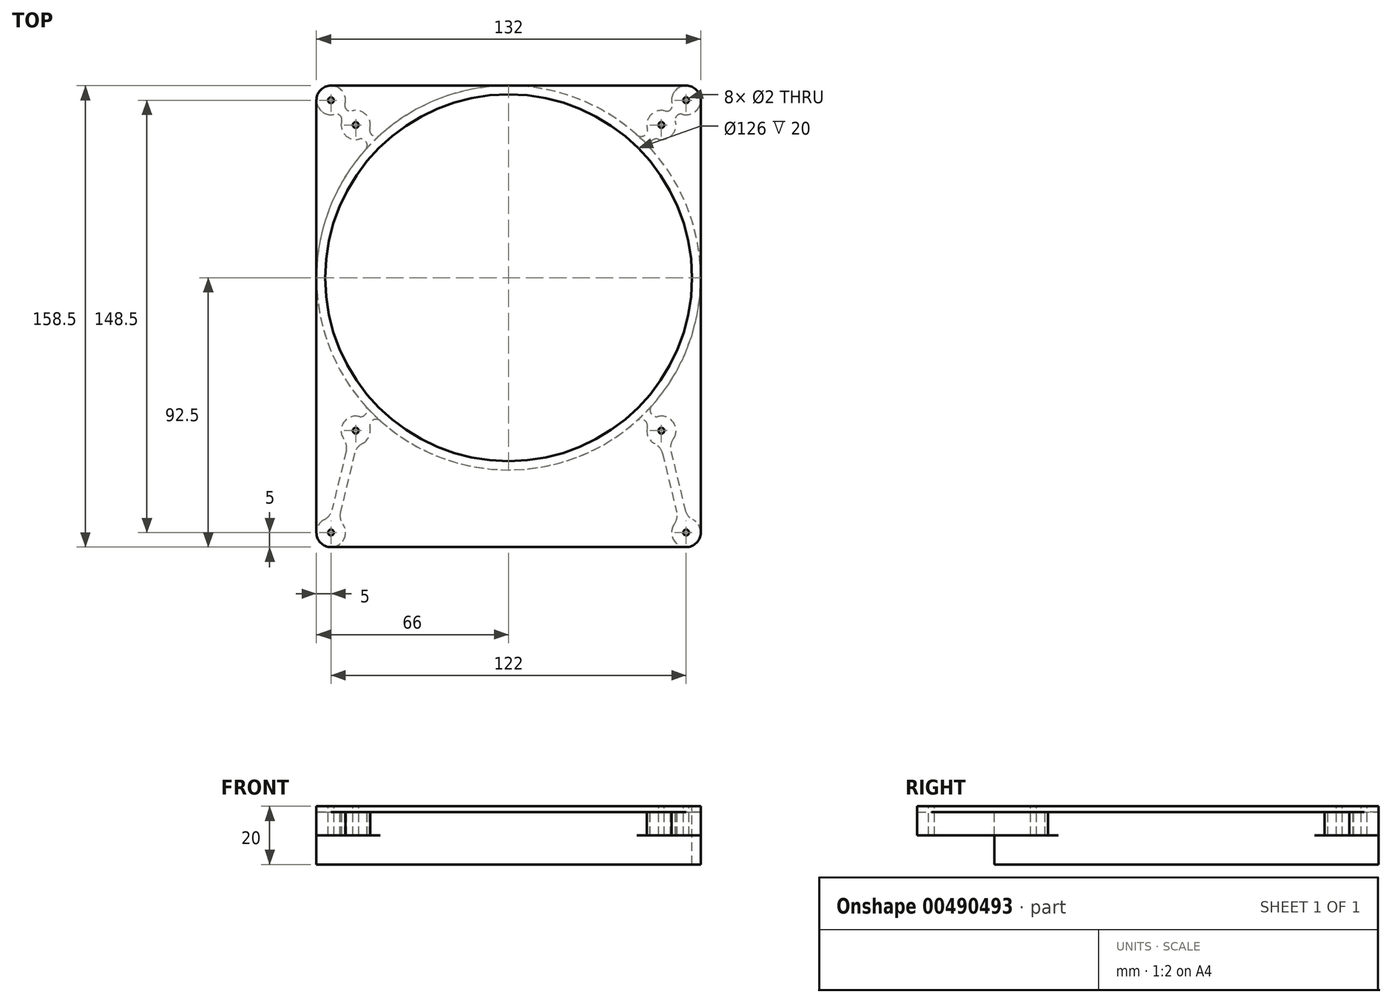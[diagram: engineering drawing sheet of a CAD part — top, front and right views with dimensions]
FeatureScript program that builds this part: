
annotation { "Feature Type Name" : "Feature", "Feature Type Description" : "" }
export const myFeature = defineFeature(function(context is Context, id is Id, definition is map)
    precondition{}
    {
        {
            var Q0;
            Q0=qCreatedBy(makeId("Top.planeOp"),FACE);
            var sketch = newSketch(context, id + "F0", { "sketchPlane" : qUnion([Q0])});
            skLineSegment(sketch, "E0.bottom", {"start": v(-54.5, -59.5) * mm, "end": v(54.5, -59.5) * mm, "construction": true});
            skLineSegment(sketch, "E0.top", {"start": v(-54.5, 59.5) * mm, "end": v(54.5, 59.5) * mm, "construction": true});
            skLineSegment(sketch, "E0.left", {"start": v(-59.5, -54.5) * mm, "end": v(-59.5, 54.5) * mm, "construction": true});
            skLineSegment(sketch, "E0.right", {"start": v(59.5, -54.5) * mm, "end": v(59.5, 54.5) * mm, "construction": true});
            skPoint(sketch, "E0.middle", {"position": v(0, 0) * mm});
            skLineSegment(sketch, "E1", {"start": v(-59.5, 59.5) * mm, "end": v(59.5, -59.5) * mm, "construction": true});
            skPoint(sketch, "E2.visualSharp", {"position": v(-59.5, 59.5) * mm});
            skArc(sketch, "E2.filletArc", {"start": v(-54.5, 59.5) * mm, "mid": v(-58.04, 58.04) * mm, "end": v(-59.5, 54.5) * mm, "construction": true});
            skPoint(sketch, "E3.visualSharp", {"position": v(59.5, 59.5) * mm});
            skArc(sketch, "E3.filletArc", {"start": v(59.5, 54.5) * mm, "mid": v(58.04, 58.04) * mm, "end": v(54.5, 59.5) * mm, "construction": true});
            skPoint(sketch, "E4.visualSharp", {"position": v(59.5, -59.5) * mm});
            skArc(sketch, "E4.filletArc", {"start": v(54.5, -59.5) * mm, "mid": v(58.04, -58.04) * mm, "end": v(59.5, -54.5) * mm, "construction": true});
            skPoint(sketch, "E5.visualSharp", {"position": v(-59.5, -59.5) * mm});
            skArc(sketch, "E5.filletArc", {"start": v(-59.5, -54.5) * mm, "mid": v(-58.04, -58.04) * mm, "end": v(-54.5, -59.5) * mm, "construction": true});
            skPoint(sketch, "E6.first.point", {"position": v(-58, 0) * mm});
            skPoint(sketch, "E6.second.point", {"position": v(0, -58) * mm});
            skPoint(sketch, "E6.third.point", {"position": v(58, 0) * mm});
            skCircle(sketch, "E7", {"center": v(0, 0) * mm, "radius": 74.25 * mm, "construction": true});
            skPoint(sketch, "E8", {"position": v(-52.5, 52.5) * mm});
            skCircle(sketch, "E9", {"center": v(-52.5, -52.5) * mm, "radius": 1 * mm});
            skCircle(sketch, "E10", {"center": v(52.5, -52.5) * mm, "radius": 1 * mm});
            skCircle(sketch, "E11", {"center": v(-52.5, 52.5) * mm, "radius": 1 * mm});
            skCircle(sketch, "E12", {"center": v(52.5, 52.5) * mm, "radius": 1 * mm});
            skCircle(sketch, "E13", {"center": v(0, 0) * mm, "radius": 63 * mm});
            skArc(sketch, "E14", {"start": v(50.75, 42.2) * mm, "mid": v(0, 66) * mm, "end": v(-50.75, 42.2) * mm});
            skLineSegment(sketch, "E15", {"start": v(-74.25, 0) * mm, "end": v(99.97, 0) * mm, "construction": true});
            skPoint(sketch, "E16.endSnap0", {"position": v(0, 59.5) * mm});
            skLineSegment(sketch, "E17", {"start": v(-61, -92.5) * mm, "end": v(61, -92.5) * mm});
            skLineSegment(sketch, "E18", {"start": v(-66, 61) * mm, "end": v(-66, -87.5) * mm});
            skLineSegment(sketch, "E19", {"start": v(0, -92.5) * mm, "end": v(0, 84.54) * mm, "construction": true});
            skLineSegment(sketch, "E20", {"start": v(-61, 66) * mm, "end": v(61, 66) * mm});
            skPoint(sketch, "E21.orphan", {"position": v(-66, 0) * mm});
            skPoint(sketch, "E22.visualSharp", {"position": v(-66, -92.5) * mm});
            skPoint(sketch, "E23.visualSharp", {"position": v(-66, 66) * mm});
            skLineSegment(sketch, "E24", {"start": v(66, 61) * mm, "end": v(66, -87.5) * mm});
            skPoint(sketch, "E25.orphan", {"position": v(66, 0) * mm});
            skPoint(sketch, "E26.visualSharp", {"position": v(66, -92.5) * mm});
            skPoint(sketch, "E27.visualSharp", {"position": v(66, 66) * mm});
            skCircle(sketch, "E28", {"center": v(-61, 61) * mm, "radius": 1 * mm});
            skLineSegment(sketch, "E29", {"start": v(66, 66) * mm, "end": v(0, 0) * mm, "construction": true});
            skLineSegment(sketch, "E30", {"start": v(-58.69, 56.57) * mm, "end": v(-47.72, 45.6) * mm, "construction": true});
            skLineSegment(sketch, "E31", {"start": v(-56.81, 58.93) * mm, "end": v(-45.6, 47.72) * mm, "construction": true});
            skPoint(sketch, "E32.visualSharp", {"position": v(-56.57, 58.69) * mm});
            skPoint(sketch, "E33.visualSharp", {"position": v(-58.69, 56.57) * mm});
            skPoint(sketch, "E34.visualSharp", {"position": v(59.75, 61.87) * mm});
            skArc(sketch, "E35.trimOffspring", {"start": v(33.51, -56.86) * mm, "mid": v(65.02, -11.31) * mm, "end": v(50.75, 42.2) * mm});
            skArc(sketch, "E36.trimOffspring", {"start": v(-32.63, -57.37) * mm, "mid": v(0.51, -66) * mm, "end": v(33.51, -56.86) * mm});
            skArc(sketch, "E37.trimOffspring", {"start": v(-50.75, 42.2) * mm, "mid": v(-64.93, -11.81) * mm, "end": v(-32.63, -57.37) * mm});
            skPoint(sketch, "E38.visualSharp", {"position": v(-45.6, 47.72) * mm});
            skPoint(sketch, "E39.visualSharp", {"position": v(-47.72, 45.6) * mm});
            skPoint(sketch, "E40.visualSharp", {"position": v(-36.5, -54.99) * mm});
            skPoint(sketch, "E41.visualSharp", {"position": v(-38.97, -53.27) * mm});
            skPoint(sketch, "E42.visualSharp", {"position": v(45.6, 47.72) * mm});
            skPoint(sketch, "E43.visualSharp", {"position": v(47.72, 45.6) * mm});
            skPoint(sketch, "E44.visualSharp", {"position": v(56.57, 58.69) * mm});
            skPoint(sketch, "E45.visualSharp", {"position": v(58.69, 56.57) * mm});
            skCircle(sketch, "E46", {"center": v(61, 61) * mm, "radius": 1 * mm});
            skArc(sketch, "E47", {"start": v(51.28, 47.65) * mm, "mid": v(56.07, 49) * mm, "end": v(57.32, 53.83) * mm});
            skArc(sketch, "E48", {"start": v(59.67, 56.18) * mm, "mid": v(57.81, 55.69) * mm, "end": v(57.32, 53.83) * mm});
            skLineSegment(sketch, "E49", {"start": v(47.72, 45.6) * mm, "end": v(58.69, 56.57) * mm, "construction": true});
            skLineSegment(sketch, "E50", {"start": v(56.57, 58.69) * mm, "end": v(45.6, 47.72) * mm, "construction": true});
            skArc(sketch, "E51", {"start": v(53.83, 57.32) * mm, "mid": v(55.69, 57.81) * mm, "end": v(56.18, 59.67) * mm});
            skArc(sketch, "E52", {"start": v(44.08, 49.12) * mm, "mid": v(46.67, 48.88) * mm, "end": v(47.65, 51.28) * mm});
            skArc(sketch, "E53", {"start": v(51.28, 47.65) * mm, "mid": v(48.88, 46.67) * mm, "end": v(49.12, 44.08) * mm});
            skArc(sketch, "E54.trimOffspring", {"start": v(59.67, 56.18) * mm, "mid": v(64.54, 64.54) * mm, "end": v(56.18, 59.67) * mm});
            skArc(sketch, "E55.trimOffspring", {"start": v(53.83, 57.32) * mm, "mid": v(49, 56.07) * mm, "end": v(47.65, 51.28) * mm});
            skArc(sketch, "E56.converted", {"start": v(-56.18, 59.67) * mm, "mid": v(-64.54, 64.54) * mm, "end": v(-59.67, 56.18) * mm});
            skArc(sketch, "E57", {"start": v(-57.32, 53.83) * mm, "mid": v(-56.07, 49) * mm, "end": v(-51.28, 47.65) * mm});
            skArc(sketch, "E58", {"start": v(-56.18, 59.67) * mm, "mid": v(-55.69, 57.81) * mm, "end": v(-53.83, 57.32) * mm});
            skArc(sketch, "E59", {"start": v(-57.32, 53.83) * mm, "mid": v(-57.81, 55.69) * mm, "end": v(-59.67, 56.18) * mm});
            skArc(sketch, "E60", {"start": v(-47.65, 51.28) * mm, "mid": v(-46.67, 48.88) * mm, "end": v(-44.08, 49.12) * mm});
            skArc(sketch, "E61", {"start": v(-49.12, 44.08) * mm, "mid": v(-48.88, 46.67) * mm, "end": v(-51.28, 47.65) * mm});
            skArc(sketch, "E62.trimOffspring", {"start": v(-47.65, 51.28) * mm, "mid": v(-49, 56.07) * mm, "end": v(-53.83, 57.32) * mm});
            skArc(sketch, "E63", {"start": v(-51.32, -47.64) * mm, "mid": v(-56.65, -49.7) * mm, "end": v(-56.55, -55.43) * mm});
            skArc(sketch, "E64", {"start": v(-51.32, -47.64) * mm, "mid": v(-48.91, -46.63) * mm, "end": v(-49.16, -44.04) * mm});
            skArc(sketch, "E65", {"start": v(-44.04, -49.16) * mm, "mid": v(-46.63, -48.91) * mm, "end": v(-47.64, -51.32) * mm});
            skArc(sketch, "E66", {"start": v(47.64, -51.32) * mm, "mid": v(47.96, -54.6) * mm, "end": v(50.24, -56.96) * mm});
            skArc(sketch, "E67", {"start": v(49.16, -44.04) * mm, "mid": v(48.91, -46.63) * mm, "end": v(51.32, -47.64) * mm});
            skArc(sketch, "E68", {"start": v(47.64, -51.32) * mm, "mid": v(46.63, -48.91) * mm, "end": v(44.04, -49.16) * mm});
            skCircle(sketch, "E69", {"center": v(61, -87.5) * mm, "radius": 1 * mm});
            skArc(sketch, "E70.converted", {"start": v(56.95, -84.57) * mm, "mid": v(62.18, -92.36) * mm, "end": v(63.26, -83.04) * mm});
            skLineSegment(sketch, "E71", {"start": v(52.5, -52.5) * mm, "end": v(61, -87.5) * mm, "construction": true});
            skLineSegment(sketch, "E72", {"start": v(52.84, -60.24) * mm, "end": v(57.75, -80.47) * mm});
            skLineSegment(sketch, "E73", {"start": v(55.75, -59.53) * mm, "end": v(60.66, -79.76) * mm});
            skArc(sketch, "E74.trimOffspring", {"start": v(56.55, -55.43) * mm, "mid": v(56.65, -49.7) * mm, "end": v(51.32, -47.64) * mm});
            skPoint(sketch, "E75.visualSharp", {"position": v(58.42, -83.22) * mm});
            skArc(sketch, "E75.filletArc", {"start": v(56.95, -84.57) * mm, "mid": v(57.8, -82.61) * mm, "end": v(57.75, -80.47) * mm});
            skPoint(sketch, "E76.visualSharp", {"position": v(61.33, -82.51) * mm});
            skArc(sketch, "E76.filletArc", {"start": v(60.66, -79.76) * mm, "mid": v(61.6, -81.69) * mm, "end": v(63.26, -83.04) * mm});
            skPoint(sketch, "E77.visualSharp", {"position": v(52.17, -57.49) * mm});
            skArc(sketch, "E77.filletArc", {"start": v(52.84, -60.24) * mm, "mid": v(51.9, -58.31) * mm, "end": v(50.24, -56.96) * mm});
            skPoint(sketch, "E78.visualSharp", {"position": v(55.08, -56.78) * mm});
            skArc(sketch, "E78.filletArc", {"start": v(56.55, -55.43) * mm, "mid": v(55.7, -57.39) * mm, "end": v(55.75, -59.53) * mm});
            skArc(sketch, "E79.converted", {"start": v(-63.26, -83.04) * mm, "mid": v(-62.18, -92.36) * mm, "end": v(-56.95, -84.57) * mm});
            skLineSegment(sketch, "E80", {"start": v(-52.5, -52.5) * mm, "end": v(-62.18, -92.36) * mm, "construction": true});
            skLineSegment(sketch, "E81", {"start": v(-55.75, -59.53) * mm, "end": v(-60.66, -79.76) * mm});
            skLineSegment(sketch, "E82", {"start": v(-52.84, -60.24) * mm, "end": v(-57.75, -80.47) * mm});
            skArc(sketch, "E83.trimOffspring", {"start": v(-50.24, -56.96) * mm, "mid": v(-47.96, -54.6) * mm, "end": v(-47.64, -51.32) * mm});
            skPoint(sketch, "E84.visualSharp", {"position": v(-52.17, -57.49) * mm});
            skArc(sketch, "E84.filletArc", {"start": v(-50.24, -56.96) * mm, "mid": v(-51.9, -58.31) * mm, "end": v(-52.84, -60.24) * mm});
            skPoint(sketch, "E85.visualSharp", {"position": v(-55.08, -56.78) * mm});
            skArc(sketch, "E85.filletArc", {"start": v(-55.75, -59.53) * mm, "mid": v(-55.7, -57.39) * mm, "end": v(-56.55, -55.43) * mm});
            skPoint(sketch, "E86.visualSharp", {"position": v(-61.33, -82.51) * mm});
            skArc(sketch, "E86.filletArc", {"start": v(-63.26, -83.04) * mm, "mid": v(-61.6, -81.69) * mm, "end": v(-60.66, -79.76) * mm});
            skPoint(sketch, "E87.visualSharp", {"position": v(-58.42, -83.22) * mm});
            skArc(sketch, "E87.filletArc", {"start": v(-57.75, -80.47) * mm, "mid": v(-57.8, -82.61) * mm, "end": v(-56.95, -84.57) * mm});
            skCircle(sketch, "E88", {"center": v(-61, -87.5) * mm, "radius": 1 * mm});
            skSolve(sketch);
        }
        {
            var Q0;
            Q0=makeQuery(id+"F0.imprint","IMPRINT",FACE,{"disambiguationData":[TD([[makeQuery(id+"F0.imprint","IMPRINT",EDGE,{"derivedFrom":sQuery(id+"F0.wireOp",EDGE,"E13")}),-1.0]])]});
            extrude(context, id + "F1", {"entities" : qUnion([Q0]), "depth" : -18 * mm});
        }
        {
            var Q0;
            Q0=makeQuery(id+"F0.imprint","IMPRINT",FACE,{"disambiguationData":[TD([[makeQuery(id+"F0.imprint","IMPRINT",EDGE,{"derivedFrom":sQuery(id+"F0.wireOp",EDGE,"E10")}),-1.0]])]});
            var Q1;
            Q1=makeQuery(id+"F0.imprint","IMPRINT",FACE,{"disambiguationData":[TD([[makeQuery(id+"F0.imprint","IMPRINT",EDGE,{"derivedFrom":sQuery(id+"F0.wireOp",EDGE,"E9")}),-1.0]])]});
            var Q2;
            Q2=makeQuery(id+"F0.imprint","IMPRINT",FACE,{"disambiguationData":[TD([[makeQuery(id+"F0.imprint","IMPRINT",EDGE,{"derivedFrom":sQuery(id+"F0.wireOp",EDGE,"E11")}),-1.0]])]});
            var Q3;
            Q3=makeQuery(id+"F0.imprint","IMPRINT",FACE,{"disambiguationData":[TD([[makeQuery(id+"F0.imprint","IMPRINT",EDGE,{"derivedFrom":sQuery(id+"F0.wireOp",EDGE,"E12")}),-1.0]])]});
            extrude(context, id + "F2", {"entities" : qUnion([Q0, Q1, Q2, Q3]), "operationType" : NewBodyOperationType.ADD, "depth" : -8 * mm});
        }
        {
            var Q0;
            {var subQ0=sQuery(id+"F0.wireOp",EDGE,"E17");Q0=makeQuery(id+"F0.imprint","IMPRINT",FACE,{"disambiguationData":[TD([[makeQuery(id+"F0.imprint","IMPRINT",EDGE,{"derivedFrom":subQ0}),1.0]])]});}
            var Q1;
            Q1=makeQuery(id+"F0.imprint","IMPRINT",FACE,{"disambiguationData":[TD([[makeQuery(id+"F0.imprint","IMPRINT",EDGE,{"derivedFrom":sQuery(id+"F0.wireOp",EDGE,"E63")}),-1.0]])]});
            var Q2;
            Q2=makeQuery(id+"F0.imprint","IMPRINT",FACE,{"disambiguationData":[TD([[makeQuery(id+"F0.imprint","IMPRINT",EDGE,{"derivedFrom":sQuery(id+"F0.wireOp",EDGE,"E57")}),-1.0]])]});
            var Q3;
            {var subQ0=sQuery(id+"F0.wireOp",EDGE,"E58");Q3=makeQuery(id+"F0.imprint","IMPRINT",FACE,{"disambiguationData":[TD([[makeQuery(id+"F0.imprint","IMPRINT",EDGE,{"derivedFrom":subQ0}),1.0]])]});}
            var Q4;
            {var subQ0=sQuery(id+"F0.wireOp",EDGE,"E51");Q4=makeQuery(id+"F0.imprint","IMPRINT",FACE,{"disambiguationData":[TD([[makeQuery(id+"F0.imprint","IMPRINT",EDGE,{"derivedFrom":subQ0}),1.0]])]});}
            var Q5;
            Q5=makeQuery(id+"F0.imprint","IMPRINT",FACE,{"disambiguationData":[TD([[makeQuery(id+"F0.imprint","IMPRINT",EDGE,{"derivedFrom":sQuery(id+"F0.wireOp",EDGE,"E47")}),-1.0]])]});
            var Q6;
            {var subQ4=sQuery(id+"F0.wireOp",EDGE,"E67");Q6=makeQuery(id+"F0.imprint","IMPRINT",FACE,{"disambiguationData":[TD([[makeQuery(id+"F0.imprint","IMPRINT",EDGE,{"derivedFrom":subQ4}),1.0]])]});}
            var Q7;
            Q7=makeQuery(id+"F0.imprint","IMPRINT",FACE,{"disambiguationData":[TD([[makeQuery(id+"F0.imprint","IMPRINT",EDGE,{"derivedFrom":sQuery(id+"F0.wireOp",EDGE,"E13")}),-1.0]])]});
            var Q8;
            Q8=makeQuery(id+"F0.imprint","IMPRINT",FACE,{"disambiguationData":[TD([[makeQuery(id+"F0.imprint","IMPRINT",EDGE,{"derivedFrom":sQuery(id+"F0.wireOp",EDGE,"E10")}),-1.0]])]});
            var Q9;
            Q9=makeQuery(id+"F0.imprint","IMPRINT",FACE,{"disambiguationData":[TD([[makeQuery(id+"F0.imprint","IMPRINT",EDGE,{"derivedFrom":sQuery(id+"F0.wireOp",EDGE,"E9")}),-1.0]])]});
            var Q10;
            Q10=makeQuery(id+"F0.imprint","IMPRINT",FACE,{"disambiguationData":[TD([[makeQuery(id+"F0.imprint","IMPRINT",EDGE,{"derivedFrom":sQuery(id+"F0.wireOp",EDGE,"E11")}),-1.0]])]});
            var Q11;
            Q11=makeQuery(id+"F0.imprint","IMPRINT",FACE,{"disambiguationData":[TD([[makeQuery(id+"F0.imprint","IMPRINT",EDGE,{"derivedFrom":sQuery(id+"F0.wireOp",EDGE,"E12")}),-1.0]])]});
            extrude(context, id + "F3", {"entities" : qUnion([Q0, Q1, Q2, Q3, Q4, Q5, Q6, Q7, Q8, Q9, Q10, Q11]), "operationType" : NewBodyOperationType.ADD, "depth" : 2 * mm});
        }
    });
